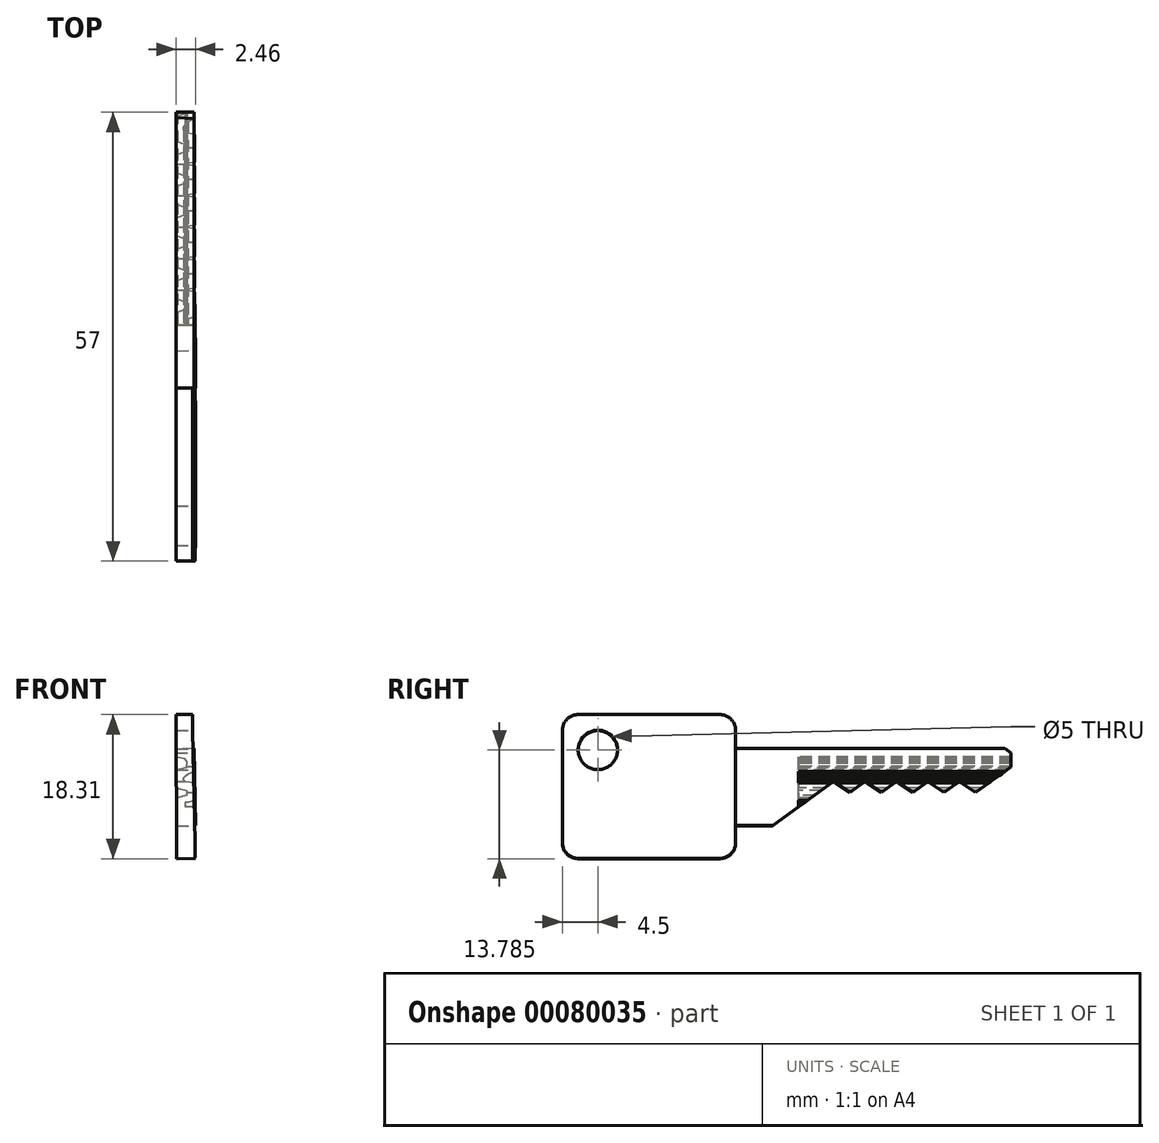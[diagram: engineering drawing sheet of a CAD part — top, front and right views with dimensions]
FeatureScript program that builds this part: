
annotation { "Feature Type Name" : "Feature", "Feature Type Description" : "" }
export const myFeature = defineFeature(function(context is Context, id is Id, definition is map)
    precondition{}
    {
        {
            var Q0;
            Q0=qCreatedBy(makeId("Front.planeOp"),FACE);
            var sketch = newSketch(context, id + "F0", { "sketchPlane" : qUnion([Q0])});
            skLineSegment(sketch, "E0", {"start": v(0.87, -6.68) * mm, "end": v(-0.75, -6.68) * mm});
            skLineSegment(sketch, "E1", {"start": v(-0.75, -6.68) * mm, "end": v(-1.23, -6.5) * mm});
            skLineSegment(sketch, "E2", {"start": v(-1.23, -6.5) * mm, "end": v(-1.23, -4.46) * mm});
            skLineSegment(sketch, "E3", {"start": v(-1.23, -4.46) * mm, "end": v(0, -4.12) * mm});
            skLineSegment(sketch, "E4", {"start": v(0, -4.12) * mm, "end": v(0, -3.52) * mm});
            skLineSegment(sketch, "E5", {"start": v(0, -3.52) * mm, "end": v(-1.26, -3.19) * mm});
            skLineSegment(sketch, "E6", {"start": v(-1.26, -3.19) * mm, "end": v(-1.26, -0.92) * mm});
            skLineSegment(sketch, "E7", {"start": v(-1.26, -0.92) * mm, "end": v(-0.1, -0.64) * mm});
            skLineSegment(sketch, "E8", {"start": v(-0.1, -0.64) * mm, "end": v(0, -0.44) * mm});
            skLineSegment(sketch, "E9", {"start": v(0, -0.44) * mm, "end": v(0.04, -0.07) * mm});
            skLineSegment(sketch, "E10", {"start": v(0.04, -0.07) * mm, "end": v(0.04, 0.11) * mm});
            skLineSegment(sketch, "E11", {"start": v(0.04, 0.11) * mm, "end": v(0, 0.26) * mm});
            skLineSegment(sketch, "E12", {"start": v(0, 0.26) * mm, "end": v(-0.18, 0.5) * mm});
            skLineSegment(sketch, "E13", {"start": v(-0.18, 0.5) * mm, "end": v(-1.16, 0.7) * mm});
            skLineSegment(sketch, "E14", {"start": v(-1.16, 0.7) * mm, "end": v(-1.4, 0.8) * mm});
            skLineSegment(sketch, "E15", {"start": v(-1.4, 0.8) * mm, "end": v(-1.35, 1.74) * mm});
            skLineSegment(sketch, "E16", {"start": v(-1.35, 1.74) * mm, "end": v(0.91, 1.81) * mm});
            skLineSegment(sketch, "E17", {"start": v(0.91, 1.81) * mm, "end": v(1, -1.1) * mm});
            skLineSegment(sketch, "E18", {"start": v(1, -1.1) * mm, "end": v(0.19, -1.38) * mm});
            skLineSegment(sketch, "E19", {"start": v(0.19, -1.38) * mm, "end": v(-0.07, -1.57) * mm});
            skLineSegment(sketch, "E20", {"start": v(-0.07, -1.57) * mm, "end": v(-0.27, -1.78) * mm});
            skLineSegment(sketch, "E21", {"start": v(-0.27, -1.78) * mm, "end": v(-0.38, -1.91) * mm});
            skLineSegment(sketch, "E22", {"start": v(-0.38, -1.91) * mm, "end": v(-0.38, -2.17) * mm});
            skLineSegment(sketch, "E23", {"start": v(-0.38, -2.17) * mm, "end": v(-0.26, -2.32) * mm});
            skLineSegment(sketch, "E24", {"start": v(-0.26, -2.32) * mm, "end": v(-0.14, -2.42) * mm});
            skLineSegment(sketch, "E25", {"start": v(-0.14, -2.42) * mm, "end": v(0.94, -2.52) * mm});
            skLineSegment(sketch, "E26", {"start": v(0.94, -2.52) * mm, "end": v(1.09, -2.63) * mm});
            skLineSegment(sketch, "E27", {"start": v(1.09, -2.63) * mm, "end": v(1.09, -4.74) * mm});
            skLineSegment(sketch, "E28", {"start": v(1.09, -4.74) * mm, "end": v(0.9, -4.86) * mm});
            skLineSegment(sketch, "E29", {"start": v(0.9, -4.86) * mm, "end": v(0.16, -5) * mm});
            skLineSegment(sketch, "E30", {"start": v(0.16, -5) * mm, "end": v(-0.2, -5) * mm});
            skLineSegment(sketch, "E31", {"start": v(-0.2, -5) * mm, "end": v(-0.2, -5.55) * mm});
            skLineSegment(sketch, "E32", {"start": v(-0.2, -5.55) * mm, "end": v(-0.2, -5.74) * mm});
            skLineSegment(sketch, "E33", {"start": v(-0.2, -5.74) * mm, "end": v(0, -5.97) * mm});
            skLineSegment(sketch, "E34", {"start": v(0, -5.97) * mm, "end": v(0.92, -6.08) * mm});
            skLineSegment(sketch, "E35", {"start": v(0.92, -6.08) * mm, "end": v(0.87, -6.68) * mm});
            skLineSegment(sketch, "E36", {"start": v(1.6, 1.81) * mm, "end": v(1.87, -6.68) * mm});
            skLineSegment(sketch, "E37", {"start": v(-1.35, 1.74) * mm, "end": v(-1.23, -8) * mm});
            skPoint(sketch, "E37.endSnap0", {"position": v(-1.23, -5.48) * mm});
            skLineSegment(sketch, "E38", {"start": v(-1.23, -8) * mm, "end": v(1.1, -7.97) * mm});
            skLineSegment(sketch, "E39", {"start": v(1.1, -7.97) * mm, "end": v(0.91, 1.81) * mm});
            skSolve(sketch);
        }
        {
            var Q0;
            Q0=makeQuery(id+"F0.imprint","IMPRINT",FACE,{"disambiguationData":[TD([[makeQuery(id+"F0.imprint","IMPRINT",EDGE,{"derivedFrom":sQuery(id+"F0.wireOp",EDGE,"E0")}),-1.0]])]});
            extrude(context, id + "F1", {"entities" : qUnion([Q0]), "oppositeDirection" : true, "depth" : 27 * mm});
        }
        {
            var Q0;
            Q0=makeQuery(id+"F0.imprint","IMPRINT",FACE,{"disambiguationData":[TD([[makeQuery(id+"F0.imprint","IMPRINT",EDGE,{"derivedFrom":sQuery(id+"F0.wireOp",EDGE,"E0")}),-1.0]])]});
            var Q1;
            Q1=makeQuery(id+"F0.imprint","IMPRINT",FACE,{"disambiguationData":[TD([[makeQuery(id+"F0.imprint","IMPRINT",EDGE,{"derivedFrom":sQuery(id+"F0.wireOp",EDGE,"E0")}),1.0]])]});
            var Q2;
            {var subQ0=sQuery(id+"F0.wireOp",EDGE,"E19");Q2=makeQuery(id+"F0.imprint","IMPRINT",FACE,{"disambiguationData":[TD([[makeQuery(id+"F0.imprint","IMPRINT",EDGE,{"derivedFrom":subQ0}),1.0]])]});}
            extrude(context, id + "F2", {"entities" : qUnion([Q0, Q1, Q2]), "operationType" : NewBodyOperationType.ADD, "depth" : 8 * mm});
        }
        {
            var Q0;
            Q0=makeQuery(id+"F2.opExtrude","CAP_FACE",FACE,{"disambiguationData":[OSD([sQuery(id+"F0.wireOp",EDGE,"E16"),sQuery(id+"F0.wireOp",EDGE,"E37"),sQuery(id+"F0.wireOp",EDGE,"E38"),sQuery(id+"F0.wireOp",EDGE,"E39")])],"isStart":false});
            var sketch = newSketch(context, id + "F3", { "sketchPlane" : qUnion([Q0])});
            skLineSegment(sketch, "E40", {"start": v(-1.35, 6.14) * mm, "end": v(0.74, 6.14) * mm});
            skLineSegment(sketch, "E41", {"start": v(0.74, 6.14) * mm, "end": v(1.1, -12.13) * mm});
            skLineSegment(sketch, "E42", {"start": v(1.1, -12.13) * mm, "end": v(-1.26, -12.17) * mm});
            skLineSegment(sketch, "E43", {"start": v(-1.26, -12.17) * mm, "end": v(-1.35, 6.14) * mm});
            skSolve(sketch);
        }
        {
            var Q0;
            {var subQ0=sQuery(id+"F3.wireOp",EDGE,"E40");Q0=makeQuery(id+"F3.imprint","IMPRINT",FACE,{"disambiguationData":[TD([[makeQuery(id+"F3.imprint","IMPRINT",EDGE,{"derivedFrom":subQ0}),-1.0]])]});}
            var Q1;
            {var subQ5=sQuery(id+"F3.wireOp",EDGE,"E41");var subQ6=makeQuery(id+"F2.opExtrude","CAP_EDGE",EDGE,{"disambiguationData":[OSD([sQuery(id+"F0.wireOp",EDGE,"E16")])],"isStart":false});var subQ7=makeQuery(id+"F3.imprint","INTERSECT",VERTEX,{"derivedFrom":[subQ6,subQ5]});Q1=makeQuery(id+"F3.imprint","IMPRINT",FACE,{"disambiguationData":[TD([[makeQuery(id+"F3.imprint","IMPRINT",EDGE,{"disambiguationData":[TD([[subQ7,-1.0]])],"derivedFrom":subQ5}),-1.0]])]});}
            var Q2;
            {var subQ1=sQuery(id+"F3.wireOp",EDGE,"E42");Q2=makeQuery(id+"F3.imprint","IMPRINT",FACE,{"disambiguationData":[TD([[makeQuery(id+"F3.imprint","IMPRINT",EDGE,{"derivedFrom":subQ1}),-1.0]])]});}
            extrude(context, id + "F4", {"entities" : qUnion([Q0, Q1, Q2]), "operationType" : NewBodyOperationType.ADD, "depth" : 22 * mm});
        }
        {
            var Q0;
            Q0=makeQuery(id+"F4.opExtrude","SWEPT_FACE",FACE,{"disambiguationData":[OSD([sQuery(id+"F3.wireOp",EDGE,"E41")])]});
            var sketch = newSketch(context, id + "F5", { "sketchPlane" : qUnion([Q0])});
            skLineSegment(sketch, "E44", {"start": v(-33.18, -9.1) * mm, "end": v(-33.18, -16.5) * mm});
            skLineSegment(sketch, "E45", {"start": v(-33.18, -16.5) * mm, "end": v(-24.85, -16.5) * mm});
            skLineSegment(sketch, "E46", {"start": v(-24.85, -16.5) * mm, "end": v(-33.18, -9.1) * mm});
            skCircle(sketch, "E47", {"center": v(-25.5, 1.62) * mm, "radius": 2.5 * mm});
            skSolve(sketch);
        }
        {
            var Q0;
            Q0=makeQuery(id+"F4.opExtrude","CAP_EDGE",EDGE,{"disambiguationData":[OSD([sQuery(id+"F3.wireOp",EDGE,"E40")])],"isStart":false});
            var Q1;
            Q1=makeQuery(id+"F4.opExtrude","CAP_EDGE",EDGE,{"disambiguationData":[OSD([sQuery(id+"F3.wireOp",EDGE,"E42")])],"isStart":false});
            var Q2;
            Q2=makeQuery(id+"F4.opExtrude","CAP_EDGE",EDGE,{"disambiguationData":[OSD([sQuery(id+"F3.wireOp",EDGE,"E40")])],"isStart":true});
            var Q3;
            Q3=makeQuery(id+"F4.opExtrude","CAP_EDGE",EDGE,{"disambiguationData":[OSD([sQuery(id+"F3.wireOp",EDGE,"E42")])],"isStart":true});
            fillet(context, id + "F6", {"entities" : qUnion([Q0, Q1, Q2, Q3]), "radius" : 2 * mm, "tangentPropagation" : true, "allowEdgeOverflow" : false});
        }
        {
            var Q0;
            Q0=qCreatedBy(makeId("Right.planeOp"),FACE);
            var sketch = newSketch(context, id + "F7", { "sketchPlane" : qUnion([Q0])});
            skLineSegment(sketch, "E48", {"start": v(0, 1.81) * mm, "end": v(4.42, 1.81) * mm});
            skLineSegment(sketch, "E49", {"start": v(4.42, -2.39) * mm, "end": v(6.5, -3.78) * mm});
            skLineSegment(sketch, "E50", {"start": v(4.42, -2.39) * mm, "end": v(-11.76, -14.14) * mm});
            skLineSegment(sketch, "E51", {"start": v(8.42, -2.39) * mm, "end": v(6.5, -3.78) * mm});
            skLineSegment(sketch, "E52", {"start": v(8.42, -2.39) * mm, "end": v(10.5, -3.78) * mm});
            skLineSegment(sketch, "E53", {"start": v(12.42, -2.39) * mm, "end": v(10.5, -3.78) * mm});
            skLineSegment(sketch, "E54", {"start": v(12.42, -2.39) * mm, "end": v(14.5, -3.78) * mm});
            skLineSegment(sketch, "E55", {"start": v(16.42, -2.39) * mm, "end": v(14.5, -3.78) * mm});
            skLineSegment(sketch, "E56", {"start": v(16.42, -2.39) * mm, "end": v(18.5, -3.78) * mm});
            skLineSegment(sketch, "E57", {"start": v(20.42, -2.39) * mm, "end": v(18.5, -3.78) * mm});
            skLineSegment(sketch, "E58", {"start": v(20.42, -2.39) * mm, "end": v(22.5, -3.78) * mm});
            skLineSegment(sketch, "E59", {"start": v(32, -14.08) * mm, "end": v(-11.76, -14.14) * mm});
            skLineSegment(sketch, "E60", {"start": v(20.89, 5.4) * mm, "end": v(28.28, 0.42) * mm});
            skLineSegment(sketch, "E61", {"start": v(28.28, 0.42) * mm, "end": v(22.5, -3.78) * mm});
            skLineSegment(sketch, "E62", {"start": v(20.89, 5.4) * mm, "end": v(31.42, 5.4) * mm});
            skLineSegment(sketch, "E63", {"start": v(31.42, 5.4) * mm, "end": v(32, -14.08) * mm});
            skLineSegment(sketch, "E64.trimOffspring", {"start": v(0, -5.6) * mm, "end": v(0, 5.42) * mm});
            skPoint(sketch, "E65.orphan", {"position": v(0, -17.43) * mm});
            skSolve(sketch);
        }
        {
            var Q0;
            Q0 = qSketchRegion(id + "F7", true);
            extrude(context, id + "F8", {"entities" : qUnion([Q0]), "operationType" : NewBodyOperationType.REMOVE, "endBound" : BoundingType.SYMMETRIC, "oppositeDirection" : true, "depth" : 40 * mm});
        }
        {
            var Q0;
            Q0 = qSketchRegion(id + "F7", true);
            extrude(context, id + "F9", {"entities" : qUnion([Q0]), "operationType" : NewBodyOperationType.REMOVE, "endBound" : BoundingType.SYMMETRIC, "oppositeDirection" : true, "depth" : 25 * mm});
        }
        {
            var Q0;
            Q0=makeQuery(id+"F5.imprint","IMPRINT",FACE,{"disambiguationData":[TD([[makeQuery(id+"F5.imprint","IMPRINT",EDGE,{"derivedFrom":sQuery(id+"F5.wireOp",EDGE,"E47")}),1.0]])]});
            extrude(context, id + "F10", {"entities" : qUnion([Q0]), "operationType" : NewBodyOperationType.REMOVE, "endBound" : BoundingType.THROUGH_ALL, "oppositeDirection" : true, "depth" : 25 * mm});
        }
        {
            var Q0;
            Q0=makeQuery(id+"F7.imprint","IMPRINT",FACE,{"disambiguationData":[TD([[makeQuery(id+"F7.imprint","IMPRINT",EDGE,{"derivedFrom":sQuery(id+"F7.wireOp",EDGE,"E49")}),-1.0]])]});
            extrude(context, id + "F11", {"entities" : qUnion([Q0]), "operationType" : NewBodyOperationType.REMOVE, "endBound" : BoundingType.SYMMETRIC, "oppositeDirection" : true, "depth" : 25 * mm});
        }
    });
